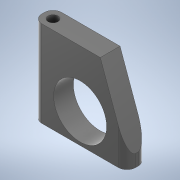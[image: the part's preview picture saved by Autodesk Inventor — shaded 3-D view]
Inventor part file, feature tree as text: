
AUTODESK INVENTOR PART (.ipt)
format: ipt  version: 2020 (Build 240168000, 168)  size: 185,344 bytes
history: native  units: mm
features: projected_geometry x9, extrude x5, sketch x4, other x1, fillet x1
ambient origin geometry x8: Origin, YZ Plane, XZ Plane, XY Plane, X Axis, Y Axis, Z Axis, Center Point
bodies: Body1 (feature_tree)
feature tree (20):
  other  "Твердое тело1"
  extrude  "Выдавливание1"  Depth=30.0mm
  fillet  "Сопряжение1"  Radius=4.0mm
  extrude  "Выдавливание2"  Depth=38.0mm
  extrude  "Выдавливание3"  Depth=8.0mm
  sketch  "Эскиз5"
  extrude  "Выдавливание4"  Depth=35.0mm TaperAngle=0.0deg
  extrude  "Выдавливание5"  Depth=3.5mm
  sketch  "Эскиз2"
  sketch  "Эскиз3"
  projected_geometry  "Спроецированная петля1"
  projected_geometry  "Спроецированная петля2"
  projected_geometry  "Спроецированная петля3"
  projected_geometry  "Спроецированная петля4"
  projected_geometry  "Спроецированная петля5"
  projected_geometry  "Спроецированная петля6"
  sketch  "Эскиз4"
  projected_geometry  "Спроецированная петля7"
  projected_geometry  "Спроецированная петля8"
  projected_geometry  "Спроецированная петля9"
